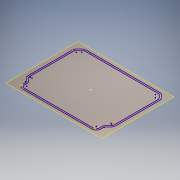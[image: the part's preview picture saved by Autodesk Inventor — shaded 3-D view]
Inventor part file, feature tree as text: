
AUTODESK INVENTOR PART (.ipt)
format: ipt  version: 2017 SP1 (Build 210196100, 196)  size: 141,312 bytes
history: native  units: mm
features: reference x65, other x3, plane x1, sketch x1
ambient origin geometry x8: Origin, YZ Plane, XZ Plane, XY Plane, X Axis, Y Axis, Z Axis, Center Point
feature tree (70):
  plane  "Arbeitsebene1"
  sketch  "Skizze7"  dims[d0=2.0mm]
  reference  "Referenz20"
  reference  "Referenz21"
  reference  "Referenz22"
  reference  "Referenz23"
  reference  "Referenz24"
  reference  "Referenz25"
  reference  "Referenz26"
  reference  "Referenz27"
  reference  "Referenz28"
  reference  "Referenz29"
  reference  "Referenz30"
  reference  "Referenz31"
  reference  "Referenz32"
  reference  "Referenz33"
  reference  "Referenz34"
  reference  "Referenz35"
  reference  "Referenz36"
  reference  "Referenz37"
  reference  "Referenz38"
  reference  "Referenz39"
  reference  "Referenz40"
  reference  "Referenz41"
  reference  "Referenz42"
  reference  "Referenz43"
  reference  "Referenz44"
  reference  "Referenz45"
  reference  "Referenz46"
  reference  "Referenz47"
  reference  "Referenz48"
  reference  "Referenz49"
  reference  "Referenz50"
  reference  "Referenz51"
  reference  "Referenz52"
  reference  "Referenz53"
  reference  "Referenz54"
  reference  "Referenz55"
  reference  "Referenz56"
  reference  "Referenz57"
  reference  "Referenz58"
  reference  "Referenz59"
  reference  "Referenz60"
  reference  "Referenz61"
  reference  "Referenz62"
  reference  "Referenz63"
  reference  "Referenz64"
  reference  "Referenz65"
  reference  "Referenz66"
  reference  "Referenz67"
  reference  "Referenz68"
  reference  "Referenz69"
  reference  "Referenz70"
  reference  "Referenz71"
  reference  "Referenz72"
  reference  "Referenz73"
  reference  "Referenz74"
  reference  "Referenz75"
  reference  "Referenz76"
  reference  "Referenz77"
  reference  "Referenz78"
  reference  "Referenz79"
  reference  "Referenz80"
  reference  "Referenz81"
  reference  "Referenz82"
  reference  "Referenz83"
  reference  "Referenz84"
  other  "<userpath>\Dropbox\Elektronik\aXe_Dashboard240XL\Gehäuse\Montiert.iam"
  other  "Montiert.iam"
  other  "GehäuseDeckel:1"
